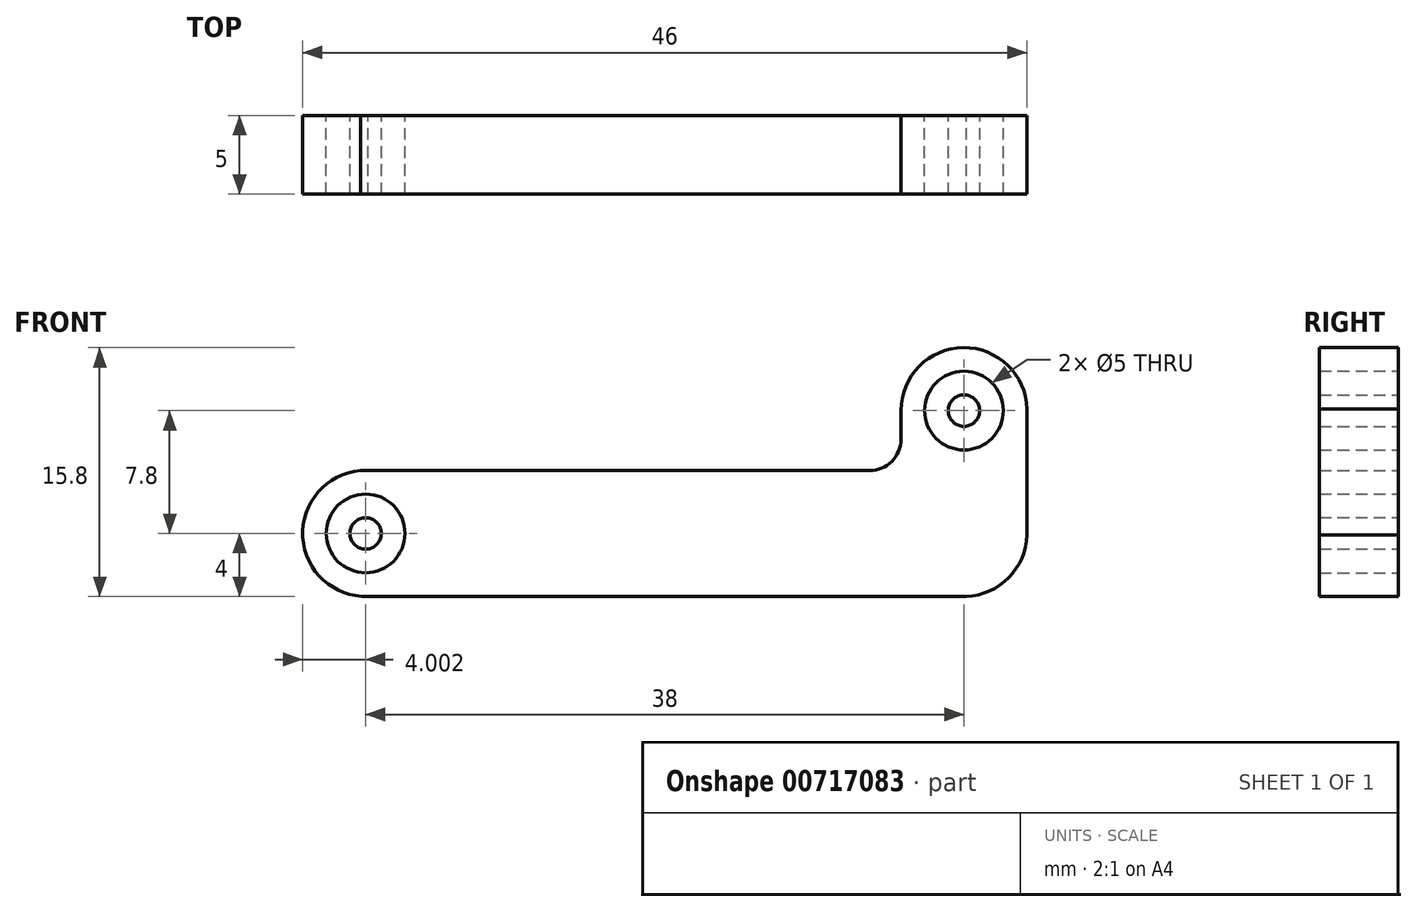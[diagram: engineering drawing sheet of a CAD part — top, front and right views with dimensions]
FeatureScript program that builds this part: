
annotation { "Feature Type Name" : "Feature", "Feature Type Description" : "" }
export const myFeature = defineFeature(function(context is Context, id is Id, definition is map)
    precondition{}
    {
        {
            var Q0;
            Q0=qCreatedBy(makeId("Front.planeOp"),FACE);
            var sketch = newSketch(context, id + "F0", { "sketchPlane" : qUnion([Q0])});
            skCircle(sketch, "E0", {"center": v(-15.85, 29.93) * mm, "radius": 2.5 * mm});
            skArc(sketch, "E1", {"start": v(-15.52, 33.92) * mm, "mid": v(-19.85, 30.02) * mm, "end": v(-15.7, 25.93) * mm});
            skArc(sketch, "E2", {"start": v(22, 25.93) * mm, "mid": v(24.96, 27.08) * mm, "end": v(26.15, 30.02) * mm});
            skCircle(sketch, "E3", {"center": v(22.15, 37.73) * mm, "radius": 2.5 * mm});
            skArc(sketch, "E4", {"start": v(26.15, 37.64) * mm, "mid": v(22.2, 41.73) * mm, "end": v(18.15, 37.73) * mm});
            skLineSegment(sketch, "E5", {"start": v(-16.18, 33.92) * mm, "end": v(16.15, 33.92) * mm});
            skLineSegment(sketch, "E6", {"start": v(-15.7, 25.93) * mm, "end": v(22.3, 25.93) * mm});
            skLineSegment(sketch, "E7", {"start": v(26.15, 37.82) * mm, "end": v(26.15, 29.84) * mm});
            skLineSegment(sketch, "E8", {"start": v(18.15, 37.73) * mm, "end": v(18.15, 35.92) * mm});
            skArc(sketch, "E9.filletArc", {"start": v(16.15, 33.92) * mm, "mid": v(17.57, 34.5) * mm, "end": v(18.15, 35.92) * mm});
            skCircle(sketch, "E10", {"center": v(-15.85, 29.93) * mm, "radius": 1 * mm});
            skCircle(sketch, "E11", {"center": v(22.15, 37.73) * mm, "radius": 1 * mm});
            skSolve(sketch);
        }
        {
            var Q0;
            Q0=makeQuery(id+"F0.imprint","IMPRINT",FACE,{"disambiguationData":[TD([[makeQuery(id+"F0.imprint","IMPRINT",EDGE,{"derivedFrom":sQuery(id+"F0.wireOp",EDGE,"E0")}),-1.0]])]});
            extrude(context, id + "F1", {"entities" : qUnion([Q0]), "depth" : 5 * mm, "offsetDistance" : 25.4 * mm});
        }
        {
            var Q0;
            Q0=makeQuery(id+"F0.imprint","IMPRINT",FACE,{"disambiguationData":[TD([[makeQuery(id+"F0.imprint","IMPRINT",EDGE,{"derivedFrom":sQuery(id+"F0.wireOp",EDGE,"E10")}),1.0]])]});
            var Q1;
            Q1=makeQuery(id+"F0.imprint","IMPRINT",FACE,{"disambiguationData":[TD([[makeQuery(id+"F0.imprint","IMPRINT",EDGE,{"derivedFrom":sQuery(id+"F0.wireOp",EDGE,"E11")}),1.0]])]});
            extrude(context, id + "F2", {"entities" : qUnion([Q0, Q1]), "depth" : 5 * mm, "offsetDistance" : 25.4 * mm});
        }
    });
